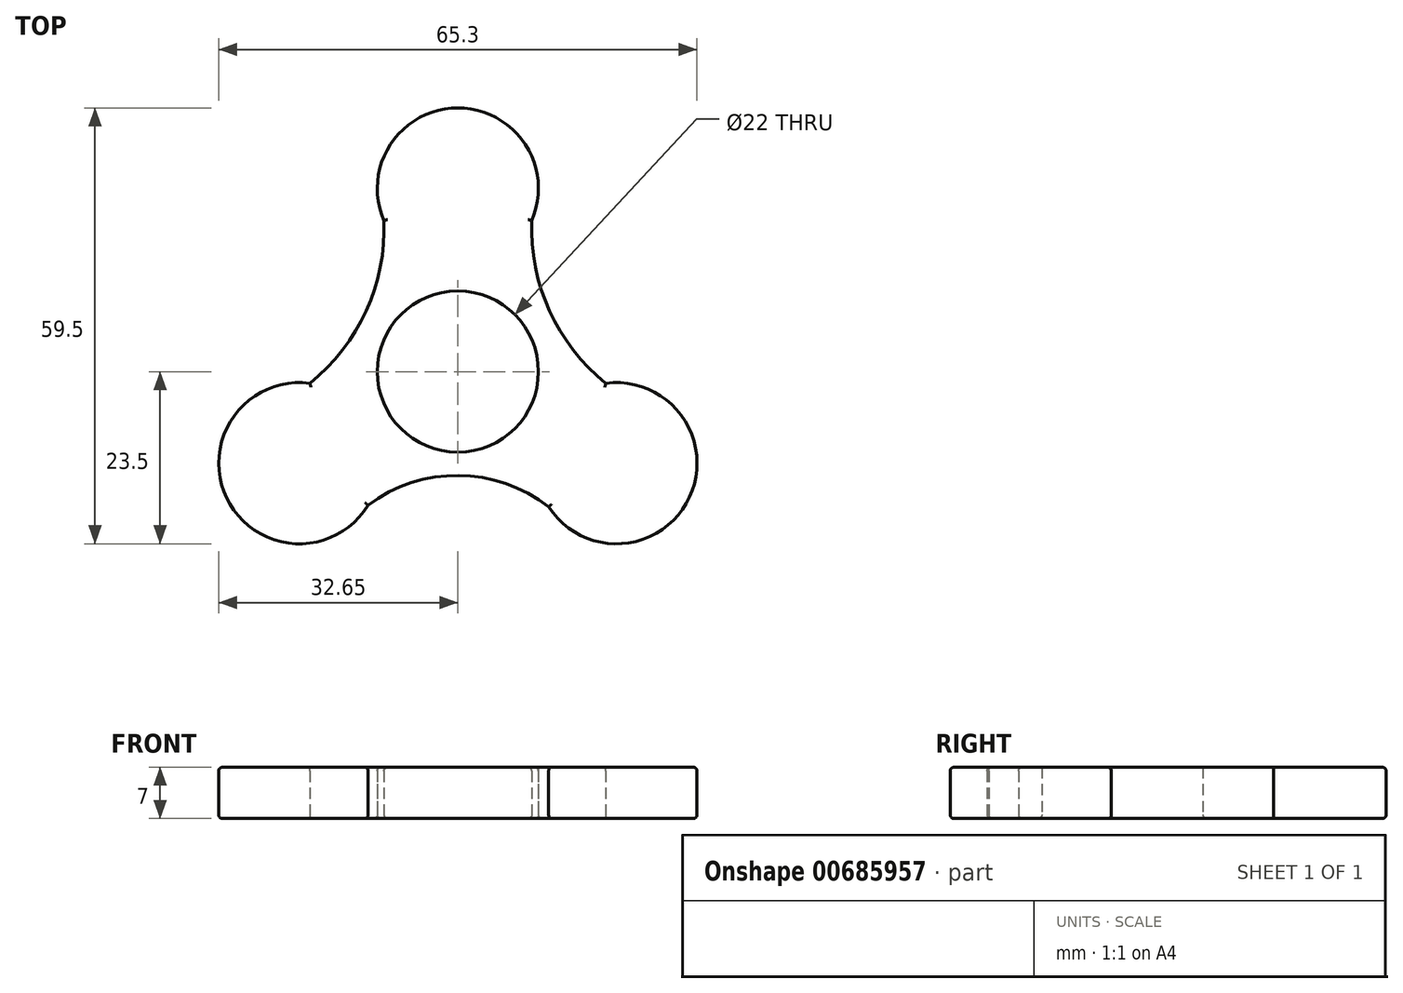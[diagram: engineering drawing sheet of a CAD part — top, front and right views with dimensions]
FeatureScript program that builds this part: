
annotation { "Feature Type Name" : "Feature", "Feature Type Description" : "" }
export const myFeature = defineFeature(function(context is Context, id is Id, definition is map)
    precondition{}
    {
        {
            var Q0;
            Q0=qCreatedBy(makeId("Top.planeOp"),FACE);
            var sketch = newSketch(context, id + "F0", { "sketchPlane" : qUnion([Q0])});
            skCircle(sketch, "E0", {"center": v(0, 0) * mm, "radius": 11 * mm});
            skArc(sketch, "E1", {"start": v(10.1, 20.64) * mm, "mid": v(0, 36) * mm, "end": v(-10.1, 20.64) * mm});
            skArc(sketch, "E2.1.0", {"start": v(-20.2, -1.6) * mm, "mid": v(-31.58, -17.23) * mm, "end": v(-12.27, -18.24) * mm});
            skArc(sketch, "E2.2.0", {"start": v(12.4, -18.45) * mm, "mid": v(31.63, -17.12) * mm, "end": v(20.2, -1.6) * mm});
            skArc(sketch, "E3", {"start": v(-20.2, -1.6) * mm, "mid": v(-12.5, 8.32) * mm, "end": v(-10.1, 20.64) * mm});
            skArc(sketch, "E4.MirrorCS", {"start": v(20.2, -1.6) * mm, "mid": v(12.5, 8.32) * mm, "end": v(10.1, 20.64) * mm});
            skArc(sketch, "E5", {"start": v(12.4, -18.45) * mm, "mid": v(0.1, -14.17) * mm, "end": v(-12.27, -18.24) * mm});
            skSolve(sketch);
        }
        {
            var Q0;
            Q0 = qSketchRegion(id + "F0", true);
            extrude(context, id + "F1", {"entities" : qUnion([Q0]), "depth" : 7 * mm, "offsetDistance" : 25 * mm});
        }
        {
            var Q0;
            Q0=makeQuery(id+"F1.opExtrude","CAP_EDGE",EDGE,{"disambiguationData":[OSD([sQuery(id+"F0.wireOp",EDGE,"E3")])],"isStart":false});
            var Q1;
            Q1=makeQuery(id+"F1.opExtrude","CAP_EDGE",EDGE,{"disambiguationData":[OSD([sQuery(id+"F0.wireOp",EDGE,"E1")])],"isStart":false});
            var Q2;
            Q2=makeQuery(id+"F1.opExtrude","CAP_EDGE",EDGE,{"disambiguationData":[OSD([sQuery(id+"F0.wireOp",EDGE,"E4.MirrorCS")])],"isStart":false});
            var Q3;
            Q3=makeQuery(id+"F1.opExtrude","CAP_EDGE",EDGE,{"disambiguationData":[OSD([sQuery(id+"F0.wireOp",EDGE,"E2.2.0")])],"isStart":false});
            var Q4;
            Q4=makeQuery(id+"F1.opExtrude","CAP_EDGE",EDGE,{"disambiguationData":[OSD([sQuery(id+"F0.wireOp",EDGE,"E5")])],"isStart":false});
            var Q5;
            Q5=makeQuery(id+"F1.opExtrude","CAP_EDGE",EDGE,{"disambiguationData":[OSD([sQuery(id+"F0.wireOp",EDGE,"E2.1.0")])],"isStart":false});
            var Q6;
            Q6=makeQuery(id+"F1.opExtrude","CAP_FACE",FACE,{"disambiguationData":[OSD([sQuery(id+"F0.wireOp",EDGE,"E0"),sQuery(id+"F0.wireOp",EDGE,"E1"),sQuery(id+"F0.wireOp",EDGE,"E2.1.0"),sQuery(id+"F0.wireOp",EDGE,"E2.2.0"),sQuery(id+"F0.wireOp",EDGE,"E3"),sQuery(id+"F0.wireOp",EDGE,"E4.MirrorCS"),sQuery(id+"F0.wireOp",EDGE,"E5")])],"isStart":true});
            var Q7;
            Q7=makeQuery(id+"F1.opExtrude","CAP_EDGE",EDGE,{"disambiguationData":[OSD([sQuery(id+"F0.wireOp",EDGE,"E4.MirrorCS")])],"isStart":true});
            var Q8;
            Q8=makeQuery(id+"F1.opExtrude","CAP_EDGE",EDGE,{"disambiguationData":[OSD([sQuery(id+"F0.wireOp",EDGE,"E2.1.0")])],"isStart":true});
            var Q9;
            Q9=makeQuery(id+"F1.opExtrude","CAP_EDGE",EDGE,{"disambiguationData":[OSD([sQuery(id+"F0.wireOp",EDGE,"E5")])],"isStart":true});
            var Q10;
            Q10=makeQuery(id+"F1.opExtrude","CAP_EDGE",EDGE,{"disambiguationData":[OSD([sQuery(id+"F0.wireOp",EDGE,"E3")])],"isStart":true});
            fillet(context, id + "F2", {"entities" : qUnion([Q0, Q1, Q2, Q3, Q4, Q5, Q6, Q7, Q8, Q9, Q10]), "radius" : .5 * mm, "tangentPropagation" : true, "allowEdgeOverflow" : false});
        }
    });
